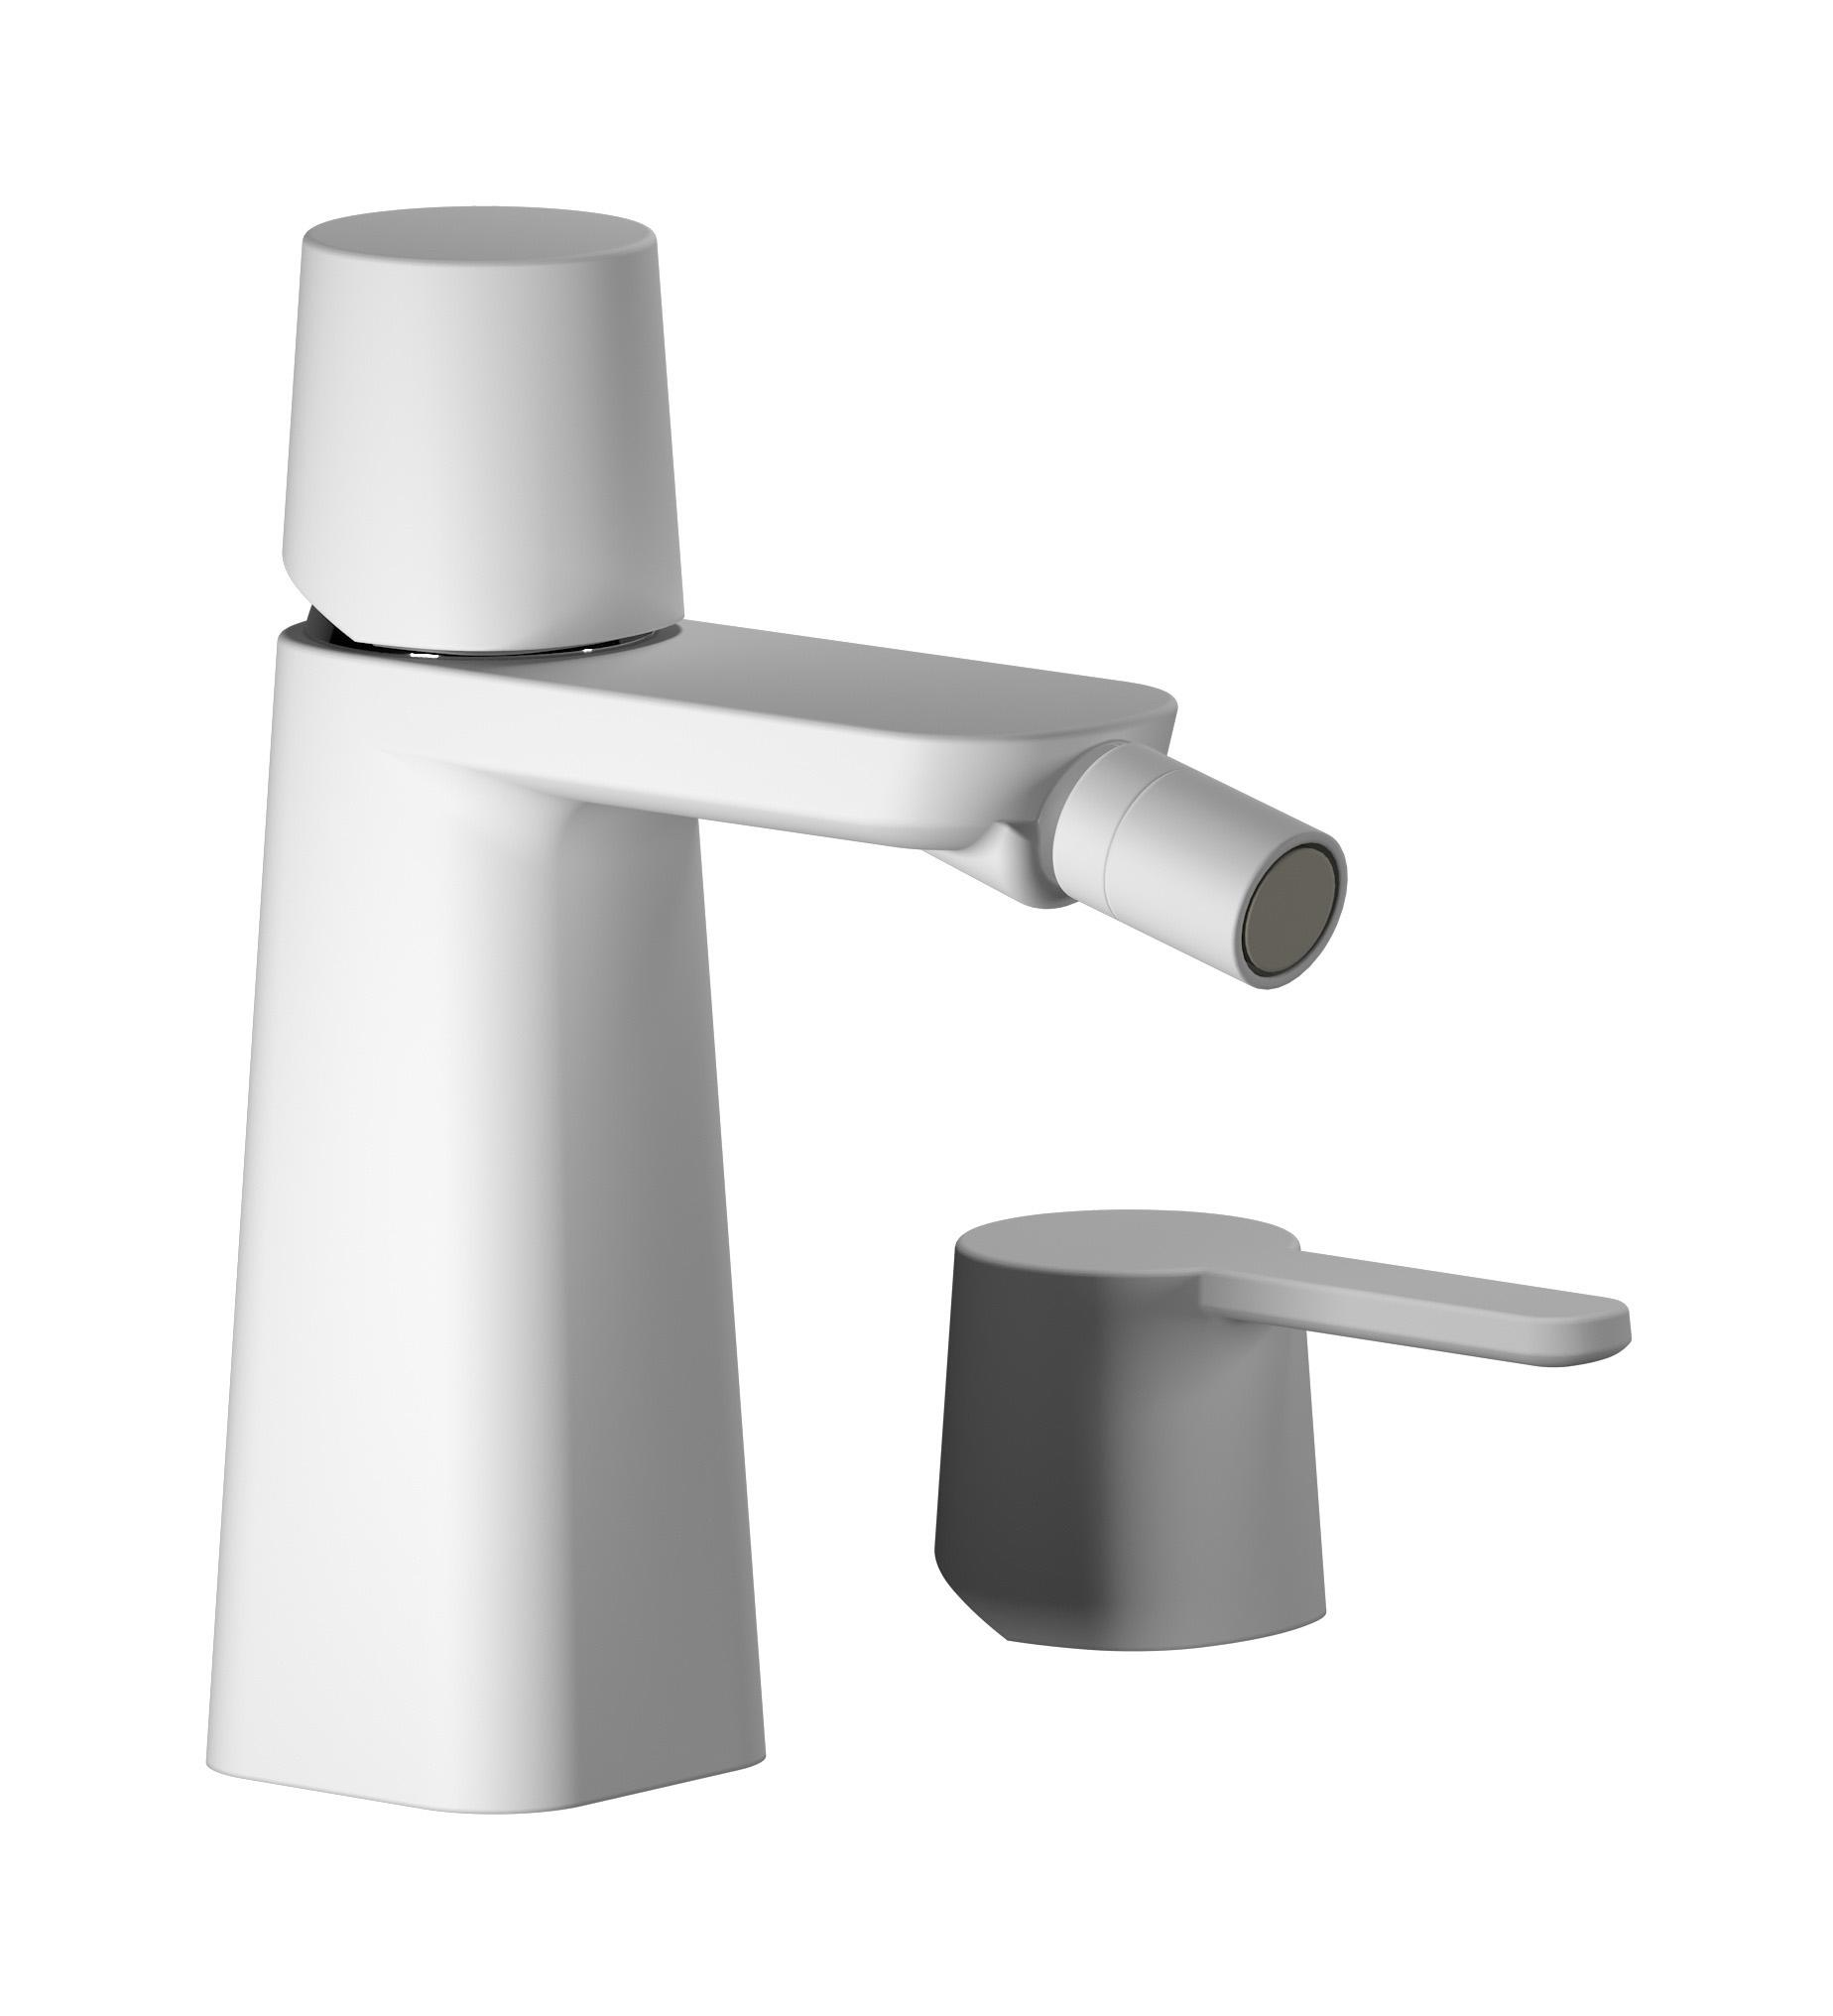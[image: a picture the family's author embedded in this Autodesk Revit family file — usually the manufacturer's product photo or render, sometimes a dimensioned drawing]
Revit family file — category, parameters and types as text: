
# Revit family: AA220
name_source: partatom
category: Apparecchi idraulici
units: mm (PartAtom-declared; Revit-internal decimal feet)

## family parameters
Basato su piano di lavoro = No
Condiviso = No
Mantieni orientamento annotazione = No
Numero OmniClass = 23.45.55.17
Punto di calcolo locali = No
Quota connettore circolare = Usa diametro
Sempre verticale = Sì
Taglio con vuoti quando caricato = No
Tipo di parte = Normale
Titolo OmniClass = Mixing Faucets

## types (5) — shared parameters
Cold water inlet = 10 mm  [stored 0.0328084 ft]
Commenti sul tipo = Bidet mixer
Connessione CW = No
Connessione HW = No
Connessione di scarico = No
Connessione di ventilazione = No
Descrizione = Monohole bidet mixer complete with drain
Hot water inlet = 10 mm  [stored 0.0328084 ft]
Produttore = IB Rubinetterie S.p.A.
URL = https://www.weareib.it
zero-valued in all types: Prospetto di default

## per-type parameters (varying)
| type | Finishes surface | Immagine tipo | Modello |
| Chrome | IB_Chrome | AA220CC.jpg | AA220CC |
| Brushed nickel | IB_Brushed nickel | AA220SS.jpg | AA220SS |
| Matt black | IB_matt black | AA220NP.jpg | AA220NP |
| Matt white | IB_matt white | AA220BO.jpg | AA220BO |
| Brushed gold | IB_brushed gold | AA220OS.jpg | AA220OS |

note: [stored X ft] marks values corroborated as IEEE doubles in the binary element streams (Revit-internal decimal feet)
